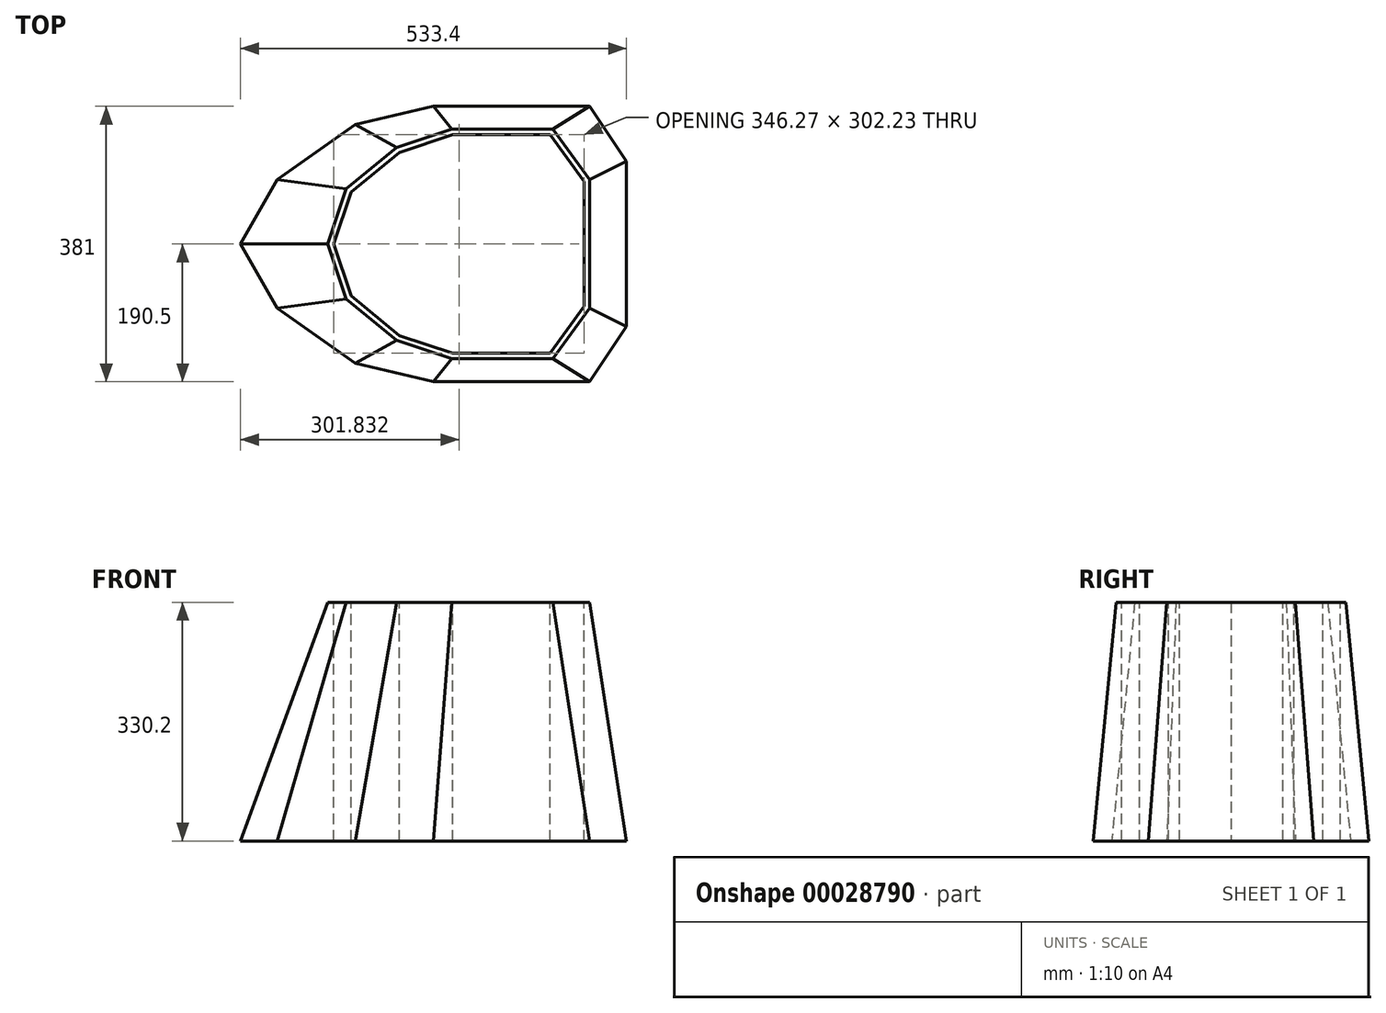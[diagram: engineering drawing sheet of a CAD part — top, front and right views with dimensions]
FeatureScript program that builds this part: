
annotation { "Feature Type Name" : "Feature", "Feature Type Description" : "" }
export const myFeature = defineFeature(function(context is Context, id is Id, definition is map)
    precondition{}
    {
        {
            var Q0;
            Q0=qCreatedBy(makeId("Top.planeOp"),FACE);
            var sketch = newSketch(context, id + "F0", { "sketchPlane" : qUnion([Q0])});
            skLineSegment(sketch, "E0.rect.bottom", {"start": v(266.7, 190.5) * mm, "end": v(-266.7, 190.5) * mm});
            skLineSegment(sketch, "E0.rect.top", {"start": v(266.7, -190.5) * mm, "end": v(-266.7, -190.5) * mm});
            skLineSegment(sketch, "E0.rect.left", {"start": v(266.7, 190.5) * mm, "end": v(266.7, -190.5) * mm});
            skLineSegment(sketch, "E0.rect.right", {"start": v(-266.7, 190.5) * mm, "end": v(-266.7, -190.5) * mm});
            skPoint(sketch, "E0.rect.middle", {"position": v(0, 0) * mm});
            skLineSegment(sketch, "E1", {"start": v(-266.7, 0) * mm, "end": v(266.7, 0) * mm, "construction": true});
            skLineSegment(sketch, "E2", {"start": v(215.9, -190.5) * mm, "end": v(215.9, 190.5) * mm, "construction": true});
            skLineSegment(sketch, "E3", {"start": v(0, -190.5) * mm, "end": v(0, 190.5) * mm, "construction": true});
            skLineSegment(sketch, "E4", {"start": v(-215.9, -190.5) * mm, "end": v(-215.9, 190.5) * mm, "construction": true});
            skLineSegment(sketch, "E5", {"start": v(-139.7, -190.5) * mm, "end": v(-139.7, 190.5) * mm, "construction": true});
            skLineSegment(sketch, "E6", {"start": v(-374.65, -190.5) * mm, "end": v(-374.65, 190.5) * mm, "construction": true});
            skLineSegment(sketch, "E7", {"start": v(-266.7, -88.9) * mm, "end": v(266.7, -88.9) * mm, "construction": true});
            skLineSegment(sketch, "E8", {"start": v(-266.7, 88.9) * mm, "end": v(266.7, 88.9) * mm, "construction": true});
            skLineSegment(sketch, "E9", {"start": v(-266.7, 165.1) * mm, "end": v(266.7, 165.1) * mm, "construction": true});
            skLineSegment(sketch, "E10", {"start": v(-266.7, -165.1) * mm, "end": v(266.7, -165.1) * mm, "construction": true});
            skLineSegment(sketch, "E11", {"start": v(581.6, 0) * mm, "end": v(581.6, -114.3) * mm, "construction": true});
            skLineSegment(sketch, "E12", {"start": v(581.6, 0) * mm, "end": v(581.6, 114.3) * mm, "construction": true});
            skLineSegment(sketch, "E13", {"start": v(266.7, -114.3) * mm, "end": v(215.9, -190.5) * mm});
            skLineSegment(sketch, "E14", {"start": v(266.7, 114.3) * mm, "end": v(215.9, 190.5) * mm});
            skLineSegment(sketch, "E15", {"start": v(-266.7, 0) * mm, "end": v(-215.9, -88.9) * mm});
            skLineSegment(sketch, "E16", {"start": v(-266.7, 0) * mm, "end": v(-215.9, 88.9) * mm});
            skLineSegment(sketch, "E17", {"start": v(-107.95, 190.5) * mm, "end": v(-107.95, -190.5) * mm, "construction": true});
            skLineSegment(sketch, "E18", {"start": v(-215.9, -88.9) * mm, "end": v(-107.95, -165.1) * mm});
            skLineSegment(sketch, "E19", {"start": v(-215.9, 88.9) * mm, "end": v(-107.95, 165.1) * mm});
            skLineSegment(sketch, "E20", {"start": v(-107.95, -165.1) * mm, "end": v(0, -190.5) * mm});
            skLineSegment(sketch, "E21", {"start": v(-107.95, 165.1) * mm, "end": v(0, 190.5) * mm});
            skSolve(sketch);
        }
        {
            var Q0;
            {var subQ3=sQuery(id+"F0.wireOp",EDGE,"E13");Q0=makeQuery(id+"F0.imprint","IMPRINT",FACE,{"disambiguationData":[TD([[makeQuery(id+"F0.imprint","IMPRINT",EDGE,{"derivedFrom":subQ3}),-1.0]])]});}
            cPlane(context, id + "F1", {"entities" : qUnion([Q0]), "cplaneType" : CPlaneType.OFFSET, "offset" : 330.2 * mm, "width" : 152.4 * mm, "height" : 152.4 * mm});
        }
        {
            var Q0;
            Q0=qCreatedBy(id+"F1.planeOp",FACE);
            var sketch = newSketch(context, id + "F2", { "sketchPlane" : qUnion([Q0])});
            skLineSegment(sketch, "E22.rect.bottom", {"start": v(266.7, 190.5) * mm, "end": v(-266.7, 190.5) * mm});
            skLineSegment(sketch, "E22.rect.top", {"start": v(266.7, -190.5) * mm, "end": v(-266.7, -190.5) * mm});
            skLineSegment(sketch, "E22.rect.left", {"start": v(266.7, 190.5) * mm, "end": v(266.7, -190.5) * mm});
            skLineSegment(sketch, "E22.rect.right", {"start": v(-266.7, 190.5) * mm, "end": v(-266.7, -190.5) * mm});
            skPoint(sketch, "E22.rect.middle", {"position": v(0, 0) * mm});
            skLineSegment(sketch, "E23", {"start": v(215.9, 190.5) * mm, "end": v(215.9, -190.5) * mm, "construction": true});
            skLineSegment(sketch, "E24", {"start": v(165.1, 190.5) * mm, "end": v(165.1, -190.5) * mm, "construction": true});
            skLineSegment(sketch, "E25", {"start": v(25.4, 190.5) * mm, "end": v(25.4, -190.5) * mm, "construction": true});
            skLineSegment(sketch, "E26", {"start": v(-50.8, 190.5) * mm, "end": v(-50.8, -190.5) * mm, "construction": true});
            skLineSegment(sketch, "E27", {"start": v(-146.05, 190.5) * mm, "end": v(-146.05, -190.5) * mm, "construction": true});
            skLineSegment(sketch, "E28", {"start": v(-120.65, 190.5) * mm, "end": v(-120.65, -190.5) * mm, "construction": true});
            skLineSegment(sketch, "E29", {"start": v(-266.7, 0) * mm, "end": v(266.7, 0) * mm, "construction": true});
            skLineSegment(sketch, "E30", {"start": v(266.7, 76.2) * mm, "end": v(-266.7, 76.2) * mm, "construction": true});
            skLineSegment(sketch, "E31", {"start": v(-266.7, 88.9) * mm, "end": v(266.7, 88.9) * mm, "construction": true});
            skLineSegment(sketch, "E32", {"start": v(-266.7, 133.35) * mm, "end": v(266.7, 133.35) * mm, "construction": true});
            skLineSegment(sketch, "E33", {"start": v(-266.7, 158.75) * mm, "end": v(266.7, 158.75) * mm, "construction": true});
            skLineSegment(sketch, "E34", {"start": v(-266.7, -88.9) * mm, "end": v(266.7, -88.9) * mm, "construction": true});
            skLineSegment(sketch, "E35", {"start": v(-266.7, -76.2) * mm, "end": v(266.7, -76.2) * mm, "construction": true});
            skLineSegment(sketch, "E36", {"start": v(-266.7, -133.35) * mm, "end": v(266.7, -133.35) * mm, "construction": true});
            skLineSegment(sketch, "E37", {"start": v(-266.7, -158.75) * mm, "end": v(266.7, -158.75) * mm, "construction": true});
            skLineSegment(sketch, "E38", {"start": v(215.9, 88.9) * mm, "end": v(165.1, 158.75) * mm});
            skLineSegment(sketch, "E39", {"start": v(165.1, 158.75) * mm, "end": v(25.4, 158.75) * mm});
            skLineSegment(sketch, "E40", {"start": v(165.1, -158.75) * mm, "end": v(25.4, -158.75) * mm});
            skLineSegment(sketch, "E41", {"start": v(25.4, 158.75) * mm, "end": v(-50.8, 133.35) * mm});
            skLineSegment(sketch, "E42", {"start": v(25.4, -158.75) * mm, "end": v(-50.8, -133.35) * mm});
            skLineSegment(sketch, "E43", {"start": v(-50.8, 133.35) * mm, "end": v(-120.65, 76.2) * mm});
            skLineSegment(sketch, "E44", {"start": v(-50.8, -133.35) * mm, "end": v(-120.65, -76.2) * mm});
            skLineSegment(sketch, "E45", {"start": v(-120.65, -76.2) * mm, "end": v(-146.05, 0) * mm});
            skLineSegment(sketch, "E46", {"start": v(-146.05, 0) * mm, "end": v(-120.65, 76.2) * mm});
            skLineSegment(sketch, "E47", {"start": v(215.9, 88.9) * mm, "end": v(215.9, -88.9) * mm});
            skLineSegment(sketch, "E48", {"start": v(215.9, -88.9) * mm, "end": v(165.1, -158.75) * mm});
            skSolve(sketch);
        }
        {
            var Q0;
            Q0=makeQuery(id+"F2.imprint","IMPRINT",FACE,{"disambiguationData":[TD([[makeQuery(id+"F2.imprint","IMPRINT",EDGE,{"derivedFrom":sQuery(id+"F2.wireOp",EDGE,"E38")}),1.0]])]});
            var Q1;
            {var subQ3=sQuery(id+"F0.wireOp",EDGE,"E13");Q1=makeQuery(id+"F0.imprint","IMPRINT",FACE,{"disambiguationData":[TD([[makeQuery(id+"F0.imprint","IMPRINT",EDGE,{"derivedFrom":subQ3}),-1.0]])]});}
            loft(context, id + "F3", {"sheetProfilesArray" : [{ "sheetProfileEntities" : qUnion([Q0]) }, { "sheetProfileEntities" : qUnion([Q1]) }]});
        }
        {
            var Q0;
            Q0=qCreatedBy(makeId("Top.planeOp"),FACE);
            cPlane(context, id + "F4", {"entities" : qUnion([Q0]), "cplaneType" : CPlaneType.OFFSET, "offset" : 95.25 * mm, "width" : 152.4 * mm, "height" : 152.4 * mm});
        }
        {
            var Q0;
            Q0=qCreatedBy(id+"F4.planeOp",FACE);
            cPlane(context, id + "F5", {"entities" : qUnion([Q0]), "cplaneType" : CPlaneType.OFFSET, "offset" : 152.4 * mm, "width" : 152.4 * mm, "height" : 152.4 * mm});
        }
        {
            var Q0;
            Q0=makeQuery(id+"F3.opLoft","CAP_FACE",FACE,{"disambiguationData":[OSD([makeQuery(id+"F2.imprint","IMPRINT",FACE,{"disambiguationData":[TD([[makeQuery(id+"F2.imprint","IMPRINT",EDGE,{"derivedFrom":sQuery(id+"F2.wireOp",EDGE,"E38")}),1.0]])]})])],"isStart":true});
            var sketch = newSketch(context, id + "F6", { "sketchPlane" : qUnion([Q0])});
            skLineSegment(sketch, "E49", {"start": v(25.4, 158.75) * mm, "end": v(-50.8, 133.35) * mm, "construction": true});
            skLineSegment(sketch, "E50", {"start": v(-50.8, 133.35) * mm, "end": v(-120.65, 76.2) * mm, "construction": true});
            skLineSegment(sketch, "E51", {"start": v(-120.65, 76.2) * mm, "end": v(-146.05, 0) * mm, "construction": true});
            skLineSegment(sketch, "E52", {"start": v(-146.05, 0) * mm, "end": v(-120.65, -76.2) * mm, "construction": true});
            skLineSegment(sketch, "E53", {"start": v(-120.65, -76.2) * mm, "end": v(-50.8, -133.35) * mm, "construction": true});
            skLineSegment(sketch, "E54", {"start": v(-50.8, -133.35) * mm, "end": v(25.4, -158.75) * mm, "construction": true});
            skLineSegment(sketch, "E55", {"start": v(25.4, -158.75) * mm, "end": v(165.1, -158.75) * mm, "construction": true});
            skLineSegment(sketch, "E56", {"start": v(165.1, -158.75) * mm, "end": v(215.9, -88.9) * mm, "construction": true});
            skLineSegment(sketch, "E57", {"start": v(215.9, -88.9) * mm, "end": v(215.9, 88.9) * mm, "construction": true});
            skLineSegment(sketch, "E58", {"start": v(215.9, 88.9) * mm, "end": v(165.1, 158.75) * mm, "construction": true});
            skLineSegment(sketch, "E59", {"start": v(165.1, 158.75) * mm, "end": v(25.4, 158.75) * mm, "construction": true});
            skLineSegment(sketch, "E60", {"start": v(-12.7, 146.05) * mm, "end": v(-12.7, -146.05) * mm, "construction": true});
            skLineSegment(sketch, "E61", {"start": v(-85.73, 104.78) * mm, "end": v(-85.73, -104.78) * mm, "construction": true});
            skLineSegment(sketch, "E62", {"start": v(-133.35, 38.1) * mm, "end": v(-133.35, -38.1) * mm, "construction": true});
            skLineSegment(sketch, "E63", {"start": v(190.5, 123.82) * mm, "end": v(190.5, -123.82) * mm, "construction": true});
            skLineSegment(sketch, "E64", {"start": v(215.9, 0) * mm, "end": v(-146.05, 0) * mm, "construction": true});
            skLineSegment(sketch, "E65", {"start": v(95.25, 158.75) * mm, "end": v(95.25, -158.75) * mm, "construction": true});
            skSolve(sketch);
        }
        {
            var Q0;
            Q0=qCreatedBy(id+"F1.planeOp",FACE);
            var sketch = newSketch(context, id + "F7", { "sketchPlane" : qUnion([Q0])});
            skLineSegment(sketch, "E66.0", {"start": v(-47.05, -126.55) * mm, "end": v(26.64, -151.12) * mm});
            skLineSegment(sketch, "E66.1", {"start": v(-114.1, -71.7) * mm, "end": v(-47.05, -126.55) * mm});
            skLineSegment(sketch, "E66.2", {"start": v(-138, 0) * mm, "end": v(-114.1, -71.7) * mm});
            skLineSegment(sketch, "E66.3", {"start": v(-114.1, 71.7) * mm, "end": v(-138, 0) * mm});
            skLineSegment(sketch, "E66.4", {"start": v(-47.05, 126.55) * mm, "end": v(-114.1, 71.7) * mm});
            skLineSegment(sketch, "E66.5", {"start": v(26.64, -151.12) * mm, "end": v(161.21, -151.12) * mm});
            skLineSegment(sketch, "E66.6", {"start": v(161.21, -151.12) * mm, "end": v(208.27, -86.42) * mm});
            skLineSegment(sketch, "E66.7", {"start": v(208.27, -86.42) * mm, "end": v(208.27, 86.42) * mm});
            skLineSegment(sketch, "E66.8", {"start": v(208.27, 86.42) * mm, "end": v(161.21, 151.12) * mm});
            skLineSegment(sketch, "E66.9", {"start": v(161.21, 151.12) * mm, "end": v(26.64, 151.12) * mm});
            skLineSegment(sketch, "E66.10", {"start": v(26.64, 151.12) * mm, "end": v(-47.05, 126.55) * mm});
            skLineSegment(sketch, "E67", {"start": v(-138, 0) * mm, "end": v(-114.1, 71.7) * mm});
            skLineSegment(sketch, "E68", {"start": v(-47.05, 126.55) * mm, "end": v(26.64, 151.12) * mm});
            skLineSegment(sketch, "E69", {"start": v(161.21, 151.12) * mm, "end": v(208.27, 86.42) * mm});
            skLineSegment(sketch, "E70", {"start": v(208.27, -86.42) * mm, "end": v(161.21, -151.12) * mm});
            skLineSegment(sketch, "E71", {"start": v(26.64, -151.12) * mm, "end": v(-47.05, -126.55) * mm});
            skLineSegment(sketch, "E72", {"start": v(-114.1, -71.7) * mm, "end": v(-138, 0) * mm});
            skSolve(sketch);
        }
        {
            var Q0;
            Q0=makeQuery(id+"F7.imprint","IMPRINT",FACE,{"disambiguationData":[TD([[makeQuery(id+"F7.imprint","IMPRINT",EDGE,{"derivedFrom":sQuery(id+"F7.wireOp",EDGE,"E66.1")}),1.0]])]});
            extrude(context, id + "F8", {"entities" : qUnion([Q0]), "operationType" : NewBodyOperationType.REMOVE, "oppositeDirection" : true, "depth" : 1270 * mm});
        }
    });
